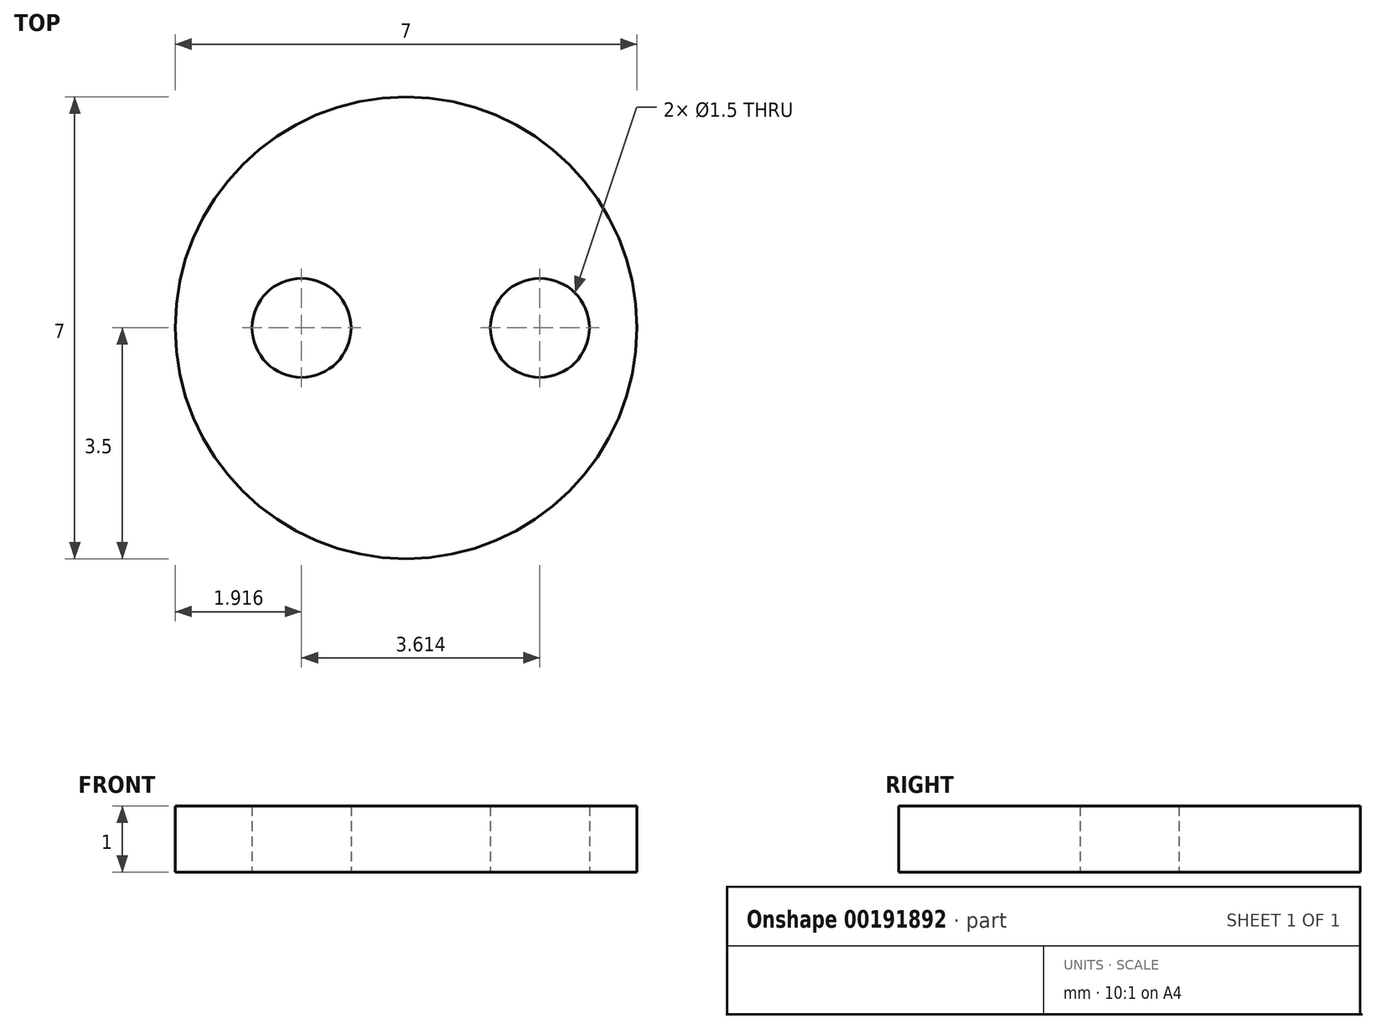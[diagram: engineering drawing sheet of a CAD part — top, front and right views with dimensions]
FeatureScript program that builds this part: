
annotation { "Feature Type Name" : "Feature", "Feature Type Description" : "" }
export const myFeature = defineFeature(function(context is Context, id is Id, definition is map)
    precondition{}
    {
        {
            var Q0;
            Q0=qCreatedBy(makeId("Top.planeOp"),FACE);
            var sketch = newSketch(context, id + "F0", { "sketchPlane" : qUnion([Q0])});
            skCircle(sketch, "E0", {"center": v(0, 0) * mm, "radius": 3.5 * mm});
            skCircle(sketch, "E1", {"center": v(-1.58, 0) * mm, "radius": 0.75 * mm});
            skCircle(sketch, "E2", {"center": v(2.03, 0) * mm, "radius": 0.75 * mm});
            skSolve(sketch);
        }
        {
            var Q0;
            Q0=makeQuery(id+"F0.imprint","IMPRINT",FACE,{"disambiguationData":[TD([[makeQuery(id+"F0.imprint","IMPRINT",EDGE,{"derivedFrom":sQuery(id+"F0.wireOp",EDGE,"E0")}),1.0]])]});
            extrude(context, id + "F1", {"entities" : qUnion([Q0]), "depth" : 1 * mm});
        }
    });
